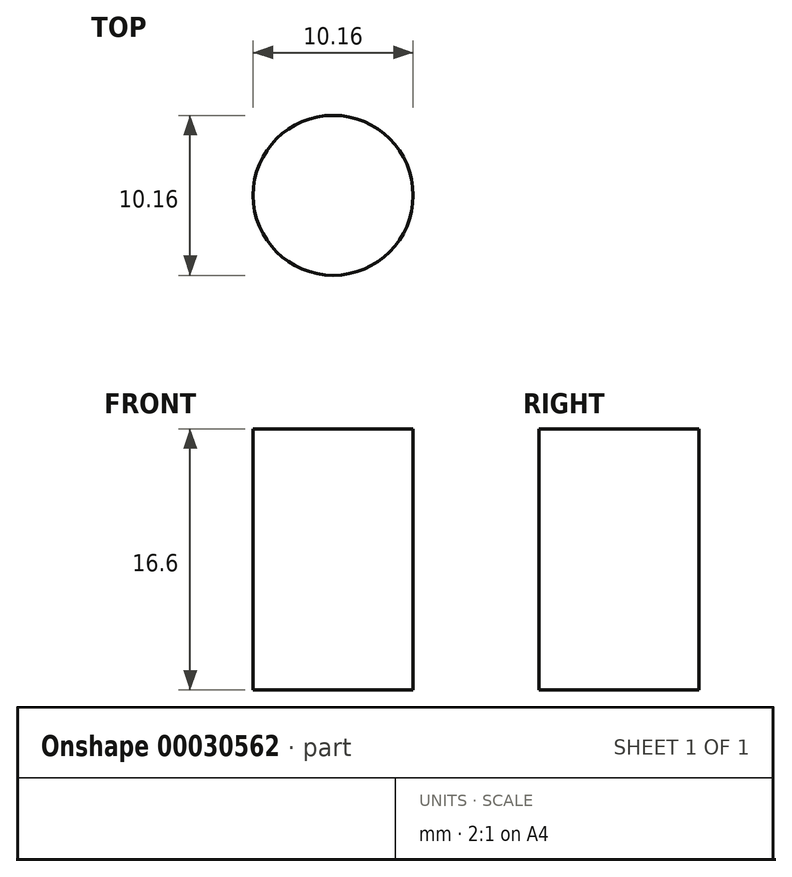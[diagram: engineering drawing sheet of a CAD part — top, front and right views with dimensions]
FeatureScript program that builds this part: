
annotation { "Feature Type Name" : "Feature", "Feature Type Description" : "" }
export const myFeature = defineFeature(function(context is Context, id is Id, definition is map)
    precondition{}
    {
        {
            var Q0;
            Q0=qCreatedBy(makeId("Front.planeOp"),FACE);
            var sketch = newSketch(context, id + "F0", { "sketchPlane" : qUnion([Q0])});
            skLineSegment(sketch, "E0", {"start": v(0, 10.54) * mm, "end": v(0, -13.1) * mm});
            skLineSegment(sketch, "E1.bottom", {"start": v(0, 10.54) * mm, "end": v(5.08, 10.54) * mm});
            skLineSegment(sketch, "E1.top", {"start": v(0, -6.06) * mm, "end": v(5.08, -6.06) * mm});
            skLineSegment(sketch, "E1.left", {"start": v(0, 10.54) * mm, "end": v(0, -6.06) * mm});
            skLineSegment(sketch, "E1.right", {"start": v(5.08, 10.54) * mm, "end": v(5.08, -6.06) * mm});
            skLineSegment(sketch, "E2", {"start": v(0, -13.1) * mm, "end": v(0, 26.9) * mm});
            skSolve(sketch);
        }
        {
            var Q0;
            Q0 = qSketchRegion(id + "F0", true);
            var Q1;
            Q1=sQuery(id+"F0.wireOp",EDGE,"E2");
            revolve(context, id + "F1", {"entities" : qUnion([Q0]), "axis" : qUnion([Q1]), "revolveType" : RevolveType.FULL});
        }
    });
